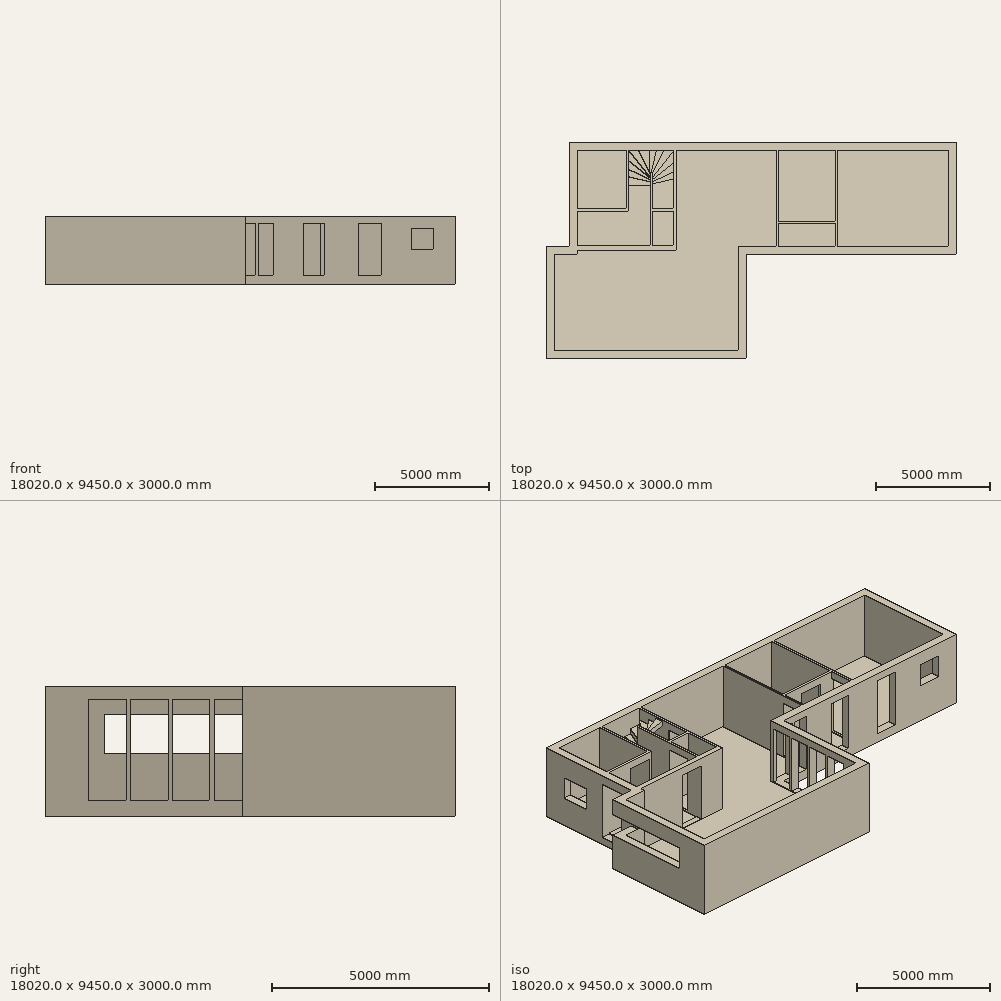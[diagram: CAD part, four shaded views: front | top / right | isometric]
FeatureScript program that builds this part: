
annotation { "Feature Type Name" : "Feature", "Feature Type Description" : "" }
export const myFeature = defineFeature(function(context is Context, id is Id, definition is map)
    precondition{}
    {
        {
            var Q0;
            Q0=qCreatedBy(makeId("Top.planeOp"),FACE);
            var sketch = newSketch(context, id + "F0", { "sketchPlane" : qUnion([Q0])});
            skLineSegment(sketch, "E0", {"start": v(1000, 0) * mm, "end": v(18020, 0) * mm});
            skLineSegment(sketch, "E1", {"start": v(18020, 0) * mm, "end": v(18020, -4900) * mm});
            skLineSegment(sketch, "E2", {"start": v(18020, -4900) * mm, "end": v(8800, -4900) * mm});
            skLineSegment(sketch, "E3", {"start": v(8800, -4900) * mm, "end": v(8800, -9450) * mm});
            skLineSegment(sketch, "E4", {"start": v(8800, -9450) * mm, "end": v(0, -9450) * mm});
            skLineSegment(sketch, "E5", {"start": v(0, -9450) * mm, "end": v(0, -4550) * mm});
            skLineSegment(sketch, "E6", {"start": v(1000, 0) * mm, "end": v(1000, -4550) * mm});
            skLineSegment(sketch, "E7", {"start": v(1000, -4550) * mm, "end": v(0, -4550) * mm});
            skSolve(sketch);
        }
        {
            var Q0;
            Q0 = qSketchRegion(id + "F0", true);
            extrude(context, id + "F1", {"entities" : qUnion([Q0]), "depth" : 3000 * mm, "offsetDistance" : 25 * mm});
        }
        {
            var Q0;
            Q0=makeQuery(id+"F1.opExtrude","CAP_FACE",FACE,{"disambiguationData":[OSD([sQuery(id+"F0.wireOp",EDGE,"E0"),sQuery(id+"F0.wireOp",EDGE,"E1"),sQuery(id+"F0.wireOp",EDGE,"E2"),sQuery(id+"F0.wireOp",EDGE,"E3"),sQuery(id+"F0.wireOp",EDGE,"E4"),sQuery(id+"F0.wireOp",EDGE,"E5")])],"isStart":false});
            shell(context, id + "F2", {"entities" : qUnion([Q0]), "thickness" : 350 * mm});
        }
        {
            var Q0;
            Q0=makeQuery(id+"F2.opShell","OFFSET_FACE",FACE,{"disambiguationData":[OSD([sQuery(id+"F0.wireOp",EDGE,"E0"),sQuery(id+"F0.wireOp",EDGE,"E1"),sQuery(id+"F0.wireOp",EDGE,"E2"),sQuery(id+"F0.wireOp",EDGE,"E3"),sQuery(id+"F0.wireOp",EDGE,"E4"),sQuery(id+"F0.wireOp",EDGE,"E5")])]});
            var sketch = newSketch(context, id + "F3", { "sketchPlane" : qUnion([Q0])});
            skLineSegment(sketch, "E8.bottom", {"start": v(1350, -4500) * mm, "end": v(5700, -4500) * mm});
            skLineSegment(sketch, "E8.top", {"start": v(1350, -4700) * mm, "end": v(5700, -4700) * mm});
            skLineSegment(sketch, "E8.left", {"start": v(1350, -4500) * mm, "end": v(1350, -4700) * mm});
            skLineSegment(sketch, "E8.right", {"start": v(5700, -4500) * mm, "end": v(5700, -4700) * mm});
            skLineSegment(sketch, "E9.bottom", {"start": v(5700, -4500) * mm, "end": v(5600, -4500) * mm});
            skLineSegment(sketch, "E9.top", {"start": v(5700, -350) * mm, "end": v(5600, -350) * mm});
            skLineSegment(sketch, "E9.left", {"start": v(5700, -4500) * mm, "end": v(5700, -350) * mm});
            skLineSegment(sketch, "E9.right", {"start": v(5600, -4500) * mm, "end": v(5600, -350) * mm});
            skLineSegment(sketch, "E10.bottom", {"start": v(1350, -3000) * mm, "end": v(3600, -3000) * mm});
            skLineSegment(sketch, "E10.top", {"start": v(1350, -2900) * mm, "end": v(3600, -2900) * mm});
            skLineSegment(sketch, "E10.left", {"start": v(1350, -3000) * mm, "end": v(1350, -2900) * mm});
            skLineSegment(sketch, "E10.right", {"start": v(3600, -3000) * mm, "end": v(3600, -2900) * mm});
            skLineSegment(sketch, "E11.bottom", {"start": v(3600, -2900) * mm, "end": v(3500, -2900) * mm});
            skLineSegment(sketch, "E11.top", {"start": v(3600, -350) * mm, "end": v(3500, -350) * mm});
            skLineSegment(sketch, "E11.left", {"start": v(3600, -2900) * mm, "end": v(3600, -350) * mm});
            skLineSegment(sketch, "E11.right", {"start": v(3500, -2900) * mm, "end": v(3500, -350) * mm});
            skLineSegment(sketch, "E12.bottom", {"start": v(5600, -3000) * mm, "end": v(4550, -3000) * mm});
            skLineSegment(sketch, "E12.top", {"start": v(5600, -2900) * mm, "end": v(4550, -2900) * mm});
            skLineSegment(sketch, "E12.left", {"start": v(5600, -3000) * mm, "end": v(5600, -2900) * mm});
            skLineSegment(sketch, "E12.right", {"start": v(4550, -3000) * mm, "end": v(4550, -2900) * mm});
            skLineSegment(sketch, "E13.bottom", {"start": v(4550, -3000) * mm, "end": v(4650, -3000) * mm});
            skLineSegment(sketch, "E13.top", {"start": v(4550, -4500) * mm, "end": v(4650, -4500) * mm});
            skLineSegment(sketch, "E13.left", {"start": v(4550, -3000) * mm, "end": v(4550, -4500) * mm});
            skLineSegment(sketch, "E13.right", {"start": v(4650, -3000) * mm, "end": v(4650, -4500) * mm});
            skLineSegment(sketch, "E14.bottom", {"start": v(10200, -4550) * mm, "end": v(10100, -4550) * mm});
            skLineSegment(sketch, "E14.top", {"start": v(10200, -350) * mm, "end": v(10100, -350) * mm});
            skLineSegment(sketch, "E14.left", {"start": v(10200, -4550) * mm, "end": v(10200, -350) * mm});
            skLineSegment(sketch, "E14.right", {"start": v(10100, -4550) * mm, "end": v(10100, -350) * mm});
            skLineSegment(sketch, "E15.bottom", {"start": v(12800, -4550) * mm, "end": v(12700, -4550) * mm});
            skLineSegment(sketch, "E15.top", {"start": v(12800, -350) * mm, "end": v(12700, -350) * mm});
            skLineSegment(sketch, "E15.left", {"start": v(12800, -4550) * mm, "end": v(12800, -350) * mm});
            skLineSegment(sketch, "E15.right", {"start": v(12700, -4550) * mm, "end": v(12700, -350) * mm});
            skLineSegment(sketch, "E16.bottom", {"start": v(10200, -3550) * mm, "end": v(12700, -3550) * mm});
            skLineSegment(sketch, "E16.top", {"start": v(10200, -3450) * mm, "end": v(12700, -3450) * mm});
            skLineSegment(sketch, "E16.left", {"start": v(10200, -3550) * mm, "end": v(10200, -3450) * mm});
            skLineSegment(sketch, "E16.right", {"start": v(12700, -3550) * mm, "end": v(12700, -3450) * mm});
            skLineSegment(sketch, "E17.bottom", {"start": v(4550, -2900) * mm, "end": v(4650, -2900) * mm});
            skLineSegment(sketch, "E17.top", {"start": v(4550, -1300) * mm, "end": v(4650, -1300) * mm});
            skLineSegment(sketch, "E17.left", {"start": v(4550, -2900) * mm, "end": v(4550, -1300) * mm});
            skLineSegment(sketch, "E17.right", {"start": v(4650, -2900) * mm, "end": v(4650, -1300) * mm});
            skSolve(sketch);
        }
        {
            var Q0;
            Q0 = qSketchRegion(id + "F3", true);
            var Q1;
            Q1=makeQuery(id+"F1.opExtrude","CAP_FACE",FACE,{"disambiguationData":[OSD([sQuery(id+"F0.wireOp",EDGE,"E0"),sQuery(id+"F0.wireOp",EDGE,"E1"),sQuery(id+"F0.wireOp",EDGE,"E2"),sQuery(id+"F0.wireOp",EDGE,"E3"),sQuery(id+"F0.wireOp",EDGE,"E4"),sQuery(id+"F0.wireOp",EDGE,"E5")])],"isStart":false});
            extrude(context, id + "F4", {"entities" : qUnion([Q0]), "operationType" : NewBodyOperationType.ADD, "endBound" : BoundingType.UP_TO_SURFACE, "depth" : 25 * mm, "endBoundEntityFace" : qUnion([Q1]), "offsetDistance" : 25 * mm});
        }
        {
            var Q0;
            {var subQ0=sQuery(id+"F0.wireOp",EDGE,"E4");var subQ1=sQuery(id+"F0.wireOp",EDGE,"E5");Q0=makeQuery(id+"F4.boolean.opBoolean","SPLIT",FACE,{"disambiguationData":[TD([makeQuery(id+"F2.opShell","OFFSET_FACE",FACE,{"disambiguationData":[OSD([subQ0])]})])],"derivedFrom":makeQuery(id+"F2.opShell","OFFSET_FACE",FACE,{"disambiguationData":[OSD([subQ1])]})});}
            var sketch = newSketch(context, id + "F5", { "sketchPlane" : qUnion([Q0])});
            skLineSegment(sketch, "E18.bottom", {"start": v(-4550, 1445.43) * mm, "end": v(-8100, 1445.43) * mm});
            skLineSegment(sketch, "E18.top", {"start": v(-4550, 2345.43) * mm, "end": v(-8100, 2345.43) * mm});
            skLineSegment(sketch, "E18.left", {"start": v(-4550, 1445.43) * mm, "end": v(-4550, 2345.43) * mm});
            skLineSegment(sketch, "E18.right", {"start": v(-8100, 1445.43) * mm, "end": v(-8100, 2345.43) * mm});
            skLineSegment(sketch, "E19.bottom", {"start": v(-4000, 380) * mm, "end": v(-3000, 380) * mm});
            skLineSegment(sketch, "E19.top", {"start": v(-4000, 2690) * mm, "end": v(-3000, 2690) * mm});
            skLineSegment(sketch, "E19.left", {"start": v(-4000, 380) * mm, "end": v(-4000, 2690) * mm});
            skLineSegment(sketch, "E19.right", {"start": v(-3000, 380) * mm, "end": v(-3000, 2690) * mm});
            skLineSegment(sketch, "E20.bottom", {"start": v(-2150, 2381.18) * mm, "end": v(-950, 2381.18) * mm});
            skLineSegment(sketch, "E20.top", {"start": v(-2150, 1481.18) * mm, "end": v(-950, 1481.18) * mm});
            skLineSegment(sketch, "E20.left", {"start": v(-2150, 2381.18) * mm, "end": v(-2150, 1481.18) * mm});
            skLineSegment(sketch, "E20.right", {"start": v(-950, 2381.18) * mm, "end": v(-950, 1481.18) * mm});
            skSolve(sketch);
        }
        {
            var Q0;
            Q0 = qSketchRegion(id + "F5", true);
            extrude(context, id + "F6", {"entities" : qUnion([Q0]), "operationType" : NewBodyOperationType.REMOVE, "endBound" : BoundingType.THROUGH_ALL, "oppositeDirection" : true, "depth" : 25 * mm, "offsetDistance" : 25 * mm});
        }
        {
            var Q0;
            Q0=makeQuery(id+"F4.opExtrude","SWEPT_FACE",FACE,{"disambiguationData":[OSD([sQuery(id+"F3.wireOp",EDGE,"E10.bottom")])]});
            var sketch = newSketch(context, id + "F7", { "sketchPlane" : qUnion([Q0])});
            skLineSegment(sketch, "E21.bottom", {"start": v(3500, 380) * mm, "end": v(2500, 380) * mm});
            skLineSegment(sketch, "E21.top", {"start": v(3500, 2690) * mm, "end": v(2500, 2690) * mm});
            skLineSegment(sketch, "E21.left", {"start": v(3500, 380) * mm, "end": v(3500, 2690) * mm});
            skLineSegment(sketch, "E21.right", {"start": v(2500, 380) * mm, "end": v(2500, 2690) * mm});
            skSolve(sketch);
        }
        {
            var Q0;
            Q0 = qSketchRegion(id + "F7", true);
            extrude(context, id + "F8", {"entities" : qUnion([Q0]), "operationType" : NewBodyOperationType.REMOVE, "endBound" : BoundingType.UP_TO_NEXT, "oppositeDirection" : true, "depth" : 25 * mm, "offsetDistance" : 25 * mm});
        }
        {
            var Q0;
            Q0=makeQuery(id+"F4.opExtrude","SWEPT_FACE",FACE,{"disambiguationData":[OSD([sQuery(id+"F3.wireOp",EDGE,"E12.right"),sQuery(id+"F3.wireOp",EDGE,"E13.left")])]});
            var sketch = newSketch(context, id + "F9", { "sketchPlane" : qUnion([Q0])});
            skLineSegment(sketch, "E22.bottom", {"start": v(4000, 380) * mm, "end": v(3000, 380) * mm});
            skLineSegment(sketch, "E22.top", {"start": v(4000, 2690) * mm, "end": v(3000, 2690) * mm});
            skLineSegment(sketch, "E22.left", {"start": v(4000, 380) * mm, "end": v(4000, 2690) * mm});
            skLineSegment(sketch, "E22.right", {"start": v(3000, 380) * mm, "end": v(3000, 2690) * mm});
            skSolve(sketch);
        }
        {
            var Q0;
            Q0 = qSketchRegion(id + "F9", true);
            extrude(context, id + "F10", {"entities" : qUnion([Q0]), "operationType" : NewBodyOperationType.REMOVE, "endBound" : BoundingType.UP_TO_NEXT, "oppositeDirection" : true, "depth" : 25 * mm, "offsetDistance" : 25 * mm});
        }
        {
            var Q0;
            Q0=makeQuery(id+"F4.opExtrude","SWEPT_FACE",FACE,{"disambiguationData":[OSD([sQuery(id+"F3.wireOp",EDGE,"E8.top")])]});
            extrude(context, id + "F11", {"entities" : qUnion([Q0]), "operationType" : NewBodyOperationType.ADD, "depth" : 25 * mm, "offsetDistance" : 25 * mm});
        }
        {
            var Q0;
            Q0=makeQuery(id+"F11.opExtrude","CAP_FACE",FACE,{"disambiguationData":[OSD([sQuery(id+"F3.wireOp",EDGE,"E8.top")])],"isStart":false});
            var sketch = newSketch(context, id + "F12", { "sketchPlane" : qUnion([Q0])});
            skLineSegment(sketch, "E23.bottom", {"start": v(4550, 380) * mm, "end": v(3550, 380) * mm});
            skLineSegment(sketch, "E23.top", {"start": v(4550, 2690) * mm, "end": v(3550, 2690) * mm});
            skLineSegment(sketch, "E23.left", {"start": v(4550, 380) * mm, "end": v(4550, 2690) * mm});
            skLineSegment(sketch, "E23.right", {"start": v(3550, 380) * mm, "end": v(3550, 2690) * mm});
            skSolve(sketch);
        }
        {
            var Q0;
            Q0 = qSketchRegion(id + "F12", true);
            extrude(context, id + "F13", {"entities" : qUnion([Q0]), "operationType" : NewBodyOperationType.REMOVE, "endBound" : BoundingType.UP_TO_NEXT, "oppositeDirection" : true, "depth" : 25 * mm, "offsetDistance" : 25 * mm});
        }
        {
            var Q0;
            Q0=makeQuery(id+"F2.opShell","OFFSET_FACE",FACE,{"disambiguationData":[OSD([sQuery(id+"F0.wireOp",EDGE,"E3")])]});
            var sketch = newSketch(context, id + "F14", { "sketchPlane" : qUnion([Q0])});
            skLineSegment(sketch, "E24.bottom", {"start": v(4700, 380) * mm, "end": v(5562.5, 380) * mm});
            skLineSegment(sketch, "E24.top", {"start": v(4700, 2690) * mm, "end": v(5562.5, 2690) * mm});
            skLineSegment(sketch, "E24.left", {"start": v(4700, 380) * mm, "end": v(4700, 2690) * mm});
            skLineSegment(sketch, "E24.right", {"start": v(5562.5, 380) * mm, "end": v(5562.5, 2690) * mm});
            skLineSegment(sketch, "E25.bottom", {"start": v(5662.5, 380) * mm, "end": v(6525, 380) * mm});
            skLineSegment(sketch, "E25.top", {"start": v(5662.5, 2690) * mm, "end": v(6525, 2690) * mm});
            skLineSegment(sketch, "E25.left", {"start": v(5662.5, 380) * mm, "end": v(5662.5, 2690) * mm});
            skLineSegment(sketch, "E25.right", {"start": v(6525, 380) * mm, "end": v(6525, 2690) * mm});
            skLineSegment(sketch, "E26.bottom", {"start": v(6625, 380) * mm, "end": v(7487.5, 380) * mm});
            skLineSegment(sketch, "E26.top", {"start": v(6625, 2690) * mm, "end": v(7487.5, 2690) * mm});
            skLineSegment(sketch, "E26.left", {"start": v(6625, 380) * mm, "end": v(6625, 2690) * mm});
            skLineSegment(sketch, "E26.right", {"start": v(7487.5, 380) * mm, "end": v(7487.5, 2690) * mm});
            skLineSegment(sketch, "E27.bottom", {"start": v(7587.5, 380) * mm, "end": v(8450, 380) * mm});
            skLineSegment(sketch, "E27.top", {"start": v(7587.5, 2690) * mm, "end": v(8450, 2690) * mm});
            skLineSegment(sketch, "E27.left", {"start": v(7587.5, 380) * mm, "end": v(7587.5, 2690) * mm});
            skLineSegment(sketch, "E27.right", {"start": v(8450, 380) * mm, "end": v(8450, 2690) * mm});
            skSolve(sketch);
        }
        {
            var Q0;
            Q0 = qSketchRegion(id + "F14", true);
            extrude(context, id + "F15", {"entities" : qUnion([Q0]), "operationType" : NewBodyOperationType.REMOVE, "oppositeDirection" : true, "depth" : 350 * mm, "offsetDistance" : 25 * mm});
        }
        {
            var Q0;
            Q0=makeQuery(id+"F1.opExtrude","SWEPT_FACE",FACE,{"disambiguationData":[OSD([sQuery(id+"F0.wireOp",EDGE,"E2")])]});
            var sketch = newSketch(context, id + "F16", { "sketchPlane" : qUnion([Q0])});
            skLineSegment(sketch, "E28.bottom", {"start": v(8600, 2690) * mm, "end": v(9250, 2690) * mm});
            skLineSegment(sketch, "E28.top", {"start": v(8600, 380) * mm, "end": v(9250, 380) * mm});
            skLineSegment(sketch, "E28.left", {"start": v(8600, 2690) * mm, "end": v(8600, 380) * mm});
            skLineSegment(sketch, "E28.right", {"start": v(9250, 2690) * mm, "end": v(9250, 380) * mm});
            skLineSegment(sketch, "E29.bottom", {"start": v(9350, 380) * mm, "end": v(10000, 380) * mm});
            skLineSegment(sketch, "E29.top", {"start": v(9350, 2690) * mm, "end": v(10000, 2690) * mm});
            skLineSegment(sketch, "E29.left", {"start": v(9350, 380) * mm, "end": v(9350, 2690) * mm});
            skLineSegment(sketch, "E29.right", {"start": v(10000, 380) * mm, "end": v(10000, 2690) * mm});
            skSolve(sketch);
        }
        {
            var Q0;
            Q0 = qSketchRegion(id + "F16", true);
            extrude(context, id + "F17", {"entities" : qUnion([Q0]), "operationType" : NewBodyOperationType.REMOVE, "oppositeDirection" : true, "depth" : 350 * mm, "offsetDistance" : 25 * mm});
        }
        {
            var Q0;
            Q0=makeQuery(id+"F4.opExtrude","SWEPT_FACE",FACE,{"disambiguationData":[OSD([sQuery(id+"F3.wireOp",EDGE,"E14.right")])]});
            var sketch = newSketch(context, id + "F18", { "sketchPlane" : qUnion([Q0])});
            skLineSegment(sketch, "E30.bottom", {"start": v(4550, 380) * mm, "end": v(3550, 380) * mm});
            skLineSegment(sketch, "E30.top", {"start": v(4550, 2690) * mm, "end": v(3550, 2690) * mm});
            skLineSegment(sketch, "E30.left", {"start": v(4550, 380) * mm, "end": v(4550, 2690) * mm});
            skLineSegment(sketch, "E30.right", {"start": v(3550, 380) * mm, "end": v(3550, 2690) * mm});
            skSolve(sketch);
        }
        {
            var Q0;
            Q0 = qSketchRegion(id + "F18", true);
            extrude(context, id + "F19", {"entities" : qUnion([Q0]), "operationType" : NewBodyOperationType.REMOVE, "oppositeDirection" : true, "depth" : 100 * mm, "offsetDistance" : 25 * mm});
        }
        {
            var Q0;
            Q0=makeQuery(id+"F4.opExtrude","SWEPT_FACE",FACE,{"disambiguationData":[OSD([sQuery(id+"F3.wireOp",EDGE,"E15.left")])]});
            var sketch = newSketch(context, id + "F20", { "sketchPlane" : qUnion([Q0])});
            skLineSegment(sketch, "E31.bottom", {"start": v(-4550, 380) * mm, "end": v(-3550, 380) * mm});
            skLineSegment(sketch, "E31.top", {"start": v(-4550, 2690) * mm, "end": v(-3550, 2690) * mm});
            skLineSegment(sketch, "E31.left", {"start": v(-4550, 380) * mm, "end": v(-4550, 2690) * mm});
            skLineSegment(sketch, "E31.right", {"start": v(-3550, 380) * mm, "end": v(-3550, 2690) * mm});
            skSolve(sketch);
        }
        {
            var Q0;
            Q0 = qSketchRegion(id + "F20", true);
            extrude(context, id + "F21", {"entities" : qUnion([Q0]), "operationType" : NewBodyOperationType.REMOVE, "endBound" : BoundingType.UP_TO_NEXT, "oppositeDirection" : true, "depth" : 25 * mm, "offsetDistance" : 25 * mm});
        }
        {
            var Q0;
            Q0=makeQuery(id+"F1.opExtrude","SWEPT_FACE",FACE,{"disambiguationData":[OSD([sQuery(id+"F0.wireOp",EDGE,"E2")])]});
            var sketch = newSketch(context, id + "F22", { "sketchPlane" : qUnion([Q0])});
            skLineSegment(sketch, "E32.bottom", {"start": v(11350, 380) * mm, "end": v(12250, 380) * mm});
            skLineSegment(sketch, "E32.top", {"start": v(11350, 2690) * mm, "end": v(12250, 2690) * mm});
            skLineSegment(sketch, "E32.left", {"start": v(11350, 380) * mm, "end": v(11350, 2690) * mm});
            skLineSegment(sketch, "E32.right", {"start": v(12250, 380) * mm, "end": v(12250, 2690) * mm});
            skLineSegment(sketch, "E33.bottom", {"start": v(16070, 2448.05) * mm, "end": v(17070, 2448.05) * mm});
            skLineSegment(sketch, "E33.top", {"start": v(16070, 1548.05) * mm, "end": v(17070, 1548.05) * mm});
            skLineSegment(sketch, "E33.left", {"start": v(16070, 2448.05) * mm, "end": v(16070, 1548.05) * mm});
            skLineSegment(sketch, "E33.right", {"start": v(17070, 2448.05) * mm, "end": v(17070, 1548.05) * mm});
            skLineSegment(sketch, "E34.bottom", {"start": v(13770, 2690) * mm, "end": v(14770, 2690) * mm});
            skLineSegment(sketch, "E34.top", {"start": v(13770, 380) * mm, "end": v(14770, 380) * mm});
            skLineSegment(sketch, "E34.left", {"start": v(13770, 2690) * mm, "end": v(13770, 380) * mm});
            skLineSegment(sketch, "E34.right", {"start": v(14770, 2690) * mm, "end": v(14770, 380) * mm});
            skSolve(sketch);
        }
        {
            var Q0;
            Q0 = qSketchRegion(id + "F22", true);
            extrude(context, id + "F23", {"entities" : qUnion([Q0]), "operationType" : NewBodyOperationType.REMOVE, "endBound" : BoundingType.UP_TO_NEXT, "oppositeDirection" : true, "depth" : 25 * mm, "offsetDistance" : 25 * mm});
        }
        {
            var Q0;
            Q0=makeQuery(id+"F4.opExtrude","SWEPT_FACE",FACE,{"disambiguationData":[OSD([sQuery(id+"F3.wireOp",EDGE,"E16.bottom")])]});
            var sketch = newSketch(context, id + "F24", { "sketchPlane" : qUnion([Q0])});
            skLineSegment(sketch, "E35.bottom", {"start": v(11100, 380) * mm, "end": v(12100, 380) * mm});
            skLineSegment(sketch, "E35.top", {"start": v(11100, 2690) * mm, "end": v(12100, 2690) * mm});
            skLineSegment(sketch, "E35.left", {"start": v(11100, 380) * mm, "end": v(11100, 2690) * mm});
            skLineSegment(sketch, "E35.right", {"start": v(12100, 380) * mm, "end": v(12100, 2690) * mm});
            skSolve(sketch);
        }
        {
            var Q0;
            Q0 = qSketchRegion(id + "F24", true);
            extrude(context, id + "F25", {"entities" : qUnion([Q0]), "operationType" : NewBodyOperationType.REMOVE, "endBound" : BoundingType.UP_TO_NEXT, "oppositeDirection" : true, "depth" : 25 * mm, "offsetDistance" : 25 * mm});
        }
        {
            var Q0;
            {var subQ0=sQuery(id+"F3.wireOp",EDGE,"E8.right");Q0=makeQuery(id+"F11.boolean.opBoolean","MERGE",FACE,{"derivedFrom":[makeQuery(id+"F4.opExtrude","SWEPT_FACE",FACE,{"disambiguationData":[OSD([subQ0,sQuery(id+"F3.wireOp",EDGE,"E9.left")])]}),makeQuery(id+"F11.opExtrude","SWEPT_FACE",FACE,{"disambiguationData":[OSD([sQuery(id+"F3.wireOp",EDGE,"E8.top"),subQ0])]})]});}
            var sketch = newSketch(context, id + "F26", { "sketchPlane" : qUnion([Q0])});
            skLineSegment(sketch, "E36.bottom", {"start": v(-1900, 380) * mm, "end": v(-2900, 380) * mm});
            skLineSegment(sketch, "E36.top", {"start": v(-1900, 2690) * mm, "end": v(-2900, 2690) * mm});
            skLineSegment(sketch, "E36.left", {"start": v(-1900, 380) * mm, "end": v(-1900, 2690) * mm});
            skLineSegment(sketch, "E36.right", {"start": v(-2900, 380) * mm, "end": v(-2900, 2690) * mm});
            skSolve(sketch);
        }
        {
            var Q0;
            Q0 = qSketchRegion(id + "F26", true);
            extrude(context, id + "F27", {"entities" : qUnion([Q0]), "operationType" : NewBodyOperationType.REMOVE, "endBound" : BoundingType.UP_TO_NEXT, "oppositeDirection" : true, "depth" : 25 * mm, "offsetDistance" : 25 * mm});
        }
        {
            var Q0;
            {var subQ1=sQuery(id+"F0.wireOp",EDGE,"E5");var subQ4=sQuery(id+"F0.wireOp",EDGE,"E0");Q0=makeQuery(id+"F4.boolean.opBoolean","SPLIT",FACE,{"disambiguationData":[TD([makeQuery(id+"F4.opExtrude","SWEPT_FACE",FACE,{"disambiguationData":[OSD([sQuery(id+"F3.wireOp",EDGE,"E10.bottom")])]})])],"derivedFrom":makeQuery(id+"F2.opShell","OFFSET_FACE",FACE,{"disambiguationData":[OSD([subQ4,sQuery(id+"F0.wireOp",EDGE,"E1"),sQuery(id+"F0.wireOp",EDGE,"E2"),sQuery(id+"F0.wireOp",EDGE,"E3"),sQuery(id+"F0.wireOp",EDGE,"E4"),subQ1])]})});}
            var sketch = newSketch(context, id + "F28", { "sketchPlane" : qUnion([Q0])});
            skLineSegment(sketch, "E37", {"start": v(4550, -1850) * mm, "end": v(3600, -1850) * mm});
            skLineSegment(sketch, "E38", {"start": v(3600, -1850) * mm, "end": v(3600, -1477.18) * mm});
            skLineSegment(sketch, "E39", {"start": v(3600, -1477.18) * mm, "end": v(4550, -1694) * mm});
            skLineSegment(sketch, "E40", {"start": v(4550, -1694) * mm, "end": v(4550, -1850) * mm});
            skSolve(sketch);
        }
        {
            var Q0;
            Q0 = qSketchRegion(id + "F28", true);
            extrude(context, id + "F29", {"entities" : qUnion([Q0]), "operationType" : NewBodyOperationType.ADD, "depth" : (3000 / 14) * mm, "offsetDistance" : 25 * mm});
        }
        {
            var Q0;
            Q0=makeQuery(id+"F29.opExtrude","CAP_FACE",FACE,{"disambiguationData":[OSD([sQuery(id+"F28.wireOp",EDGE,"E37"),sQuery(id+"F28.wireOp",EDGE,"E38"),sQuery(id+"F28.wireOp",EDGE,"E39"),sQuery(id+"F28.wireOp",EDGE,"E40")])],"isStart":false});
            var sketch = newSketch(context, id + "F30", { "sketchPlane" : qUnion([Q0])});
            skLineSegment(sketch, "E41", {"start": v(3600, -1487.43) * mm, "end": v(4550, -1704.26) * mm});
            skLineSegment(sketch, "E42", {"start": v(4550, -1704.26) * mm, "end": v(4550, -1601.6) * mm});
            skLineSegment(sketch, "E43", {"start": v(4550, -1601.6) * mm, "end": v(3600, -1144.1) * mm});
            skLineSegment(sketch, "E44", {"start": v(3600, -1144.1) * mm, "end": v(3600, -1487.43) * mm});
            skSolve(sketch);
        }
        {
            var Q0;
            Q0 = qSketchRegion(id + "F30", true);
            extrude(context, id + "F31", {"entities" : qUnion([Q0]), "operationType" : NewBodyOperationType.ADD, "depth" : (3000 / 14) * mm, "offsetDistance" : 25 * mm});
        }
        {
            var Q0;
            Q0=makeQuery(id+"F31.opExtrude","CAP_FACE",FACE,{"disambiguationData":[OSD([sQuery(id+"F30.wireOp",EDGE,"E41"),sQuery(id+"F30.wireOp",EDGE,"E42"),sQuery(id+"F30.wireOp",EDGE,"E43"),sQuery(id+"F30.wireOp",EDGE,"E44")])],"isStart":false});
            var sketch = newSketch(context, id + "F32", { "sketchPlane" : qUnion([Q0])});
            skLineSegment(sketch, "E45", {"start": v(3600, -1155.2) * mm, "end": v(4550, -1612.7) * mm});
            skLineSegment(sketch, "E46", {"start": v(4550, -1612.7) * mm, "end": v(4550, -1519.02) * mm});
            skLineSegment(sketch, "E47", {"start": v(4550, -1519.02) * mm, "end": v(3600, -761.42) * mm});
            skLineSegment(sketch, "E48", {"start": v(3600, -761.42) * mm, "end": v(3600, -1155.2) * mm});
            skSolve(sketch);
        }
        {
            var Q0;
            Q0 = qSketchRegion(id + "F32", true);
            extrude(context, id + "F33", {"entities" : qUnion([Q0]), "operationType" : NewBodyOperationType.ADD, "depth" : (3000 / 14) * mm, "offsetDistance" : 25 * mm});
        }
        {
            var Q0;
            Q0=makeQuery(id+"F33.opExtrude","CAP_FACE",FACE,{"disambiguationData":[OSD([sQuery(id+"F32.wireOp",EDGE,"E45"),sQuery(id+"F32.wireOp",EDGE,"E46"),sQuery(id+"F32.wireOp",EDGE,"E47"),sQuery(id+"F32.wireOp",EDGE,"E48")])],"isStart":false});
            var sketch = newSketch(context, id + "F34", { "sketchPlane" : qUnion([Q0])});
            skLineSegment(sketch, "E49", {"start": v(4550, -1531.81) * mm, "end": v(3600, -774.21) * mm});
            skLineSegment(sketch, "E50", {"start": v(3600, -774.21) * mm, "end": v(3600, -350) * mm});
            skLineSegment(sketch, "E51", {"start": v(3643.89, -350) * mm, "end": v(4550, -1486.23) * mm});
            skLineSegment(sketch, "E52", {"start": v(4550, -1486.23) * mm, "end": v(4550, -1531.81) * mm});
            skLineSegment(sketch, "E53", {"start": v(3600, -350) * mm, "end": v(3643.89, -350) * mm});
            skSolve(sketch);
        }
        {
            var Q0;
            Q0 = qSketchRegion(id + "F34", true);
            extrude(context, id + "F35", {"entities" : qUnion([Q0]), "operationType" : NewBodyOperationType.ADD, "depth" : (3000 / 14) * mm, "offsetDistance" : 25 * mm});
        }
        {
            var Q0;
            Q0=makeQuery(id+"F35.opExtrude","CAP_FACE",FACE,{"disambiguationData":[OSD([sQuery(id+"F34.wireOp",EDGE,"E49"),sQuery(id+"F34.wireOp",EDGE,"E50"),sQuery(id+"F34.wireOp",EDGE,"E51"),sQuery(id+"F34.wireOp",EDGE,"E52")])],"isStart":false});
            var sketch = newSketch(context, id + "F36", { "sketchPlane" : qUnion([Q0])});
            skLineSegment(sketch, "E54", {"start": v(3631.1, -350) * mm, "end": v(4550, -1502.26) * mm});
            skLineSegment(sketch, "E55", {"start": v(4550, -1502.26) * mm, "end": v(4550, -1337.24) * mm});
            skLineSegment(sketch, "E56", {"start": v(3643.89, -350) * mm, "end": v(4074.57, -350) * mm});
            skLineSegment(sketch, "E57", {"start": v(4074.57, -350) * mm, "end": v(4550, -1337.24) * mm});
            skLineSegment(sketch, "E58", {"start": v(4074.57, -350) * mm, "end": v(3631.1, -350) * mm});
            skSolve(sketch);
        }
        {
            var Q0;
            Q0 = qSketchRegion(id + "F36", true);
            extrude(context, id + "F37", {"entities" : qUnion([Q0]), "operationType" : NewBodyOperationType.ADD, "depth" : (3000 / 14) * mm, "offsetDistance" : 25 * mm});
        }
        {
            var Q0;
            Q0=makeQuery(id+"F37.opExtrude","CAP_FACE",FACE,{"disambiguationData":[OSD([sQuery(id+"F36.wireOp",EDGE,"E54"),sQuery(id+"F36.wireOp",EDGE,"E55"),sQuery(id+"F36.wireOp",EDGE,"NWCFt3wr-qczF-JT4h-rdwd-O4vbqxLeZZzJ"),sQuery(id+"F36.wireOp",EDGE,"E56"),sQuery(id+"F36.wireOp",EDGE,"E57")])],"isStart":false});
            var sketch = newSketch(context, id + "F38", { "sketchPlane" : qUnion([Q0])});
            skLineSegment(sketch, "E59", {"start": v(4063.47, -350) * mm, "end": v(4550, -1360.28) * mm});
            skLineSegment(sketch, "E60", {"start": v(4550, -1360.28) * mm, "end": v(4557.4, -1297.11) * mm});
            skLineSegment(sketch, "E61", {"start": v(4557.4, -1297.11) * mm, "end": v(4557.4, -350) * mm});
            skLineSegment(sketch, "E62", {"start": v(4557.4, -350) * mm, "end": v(4063.47, -350) * mm});
            skSolve(sketch);
        }
        {
            var Q0;
            Q0 = qSketchRegion(id + "F38", true);
            extrude(context, id + "F39", {"entities" : qUnion([Q0]), "operationType" : NewBodyOperationType.ADD, "depth" : (3000 / 14) * mm, "offsetDistance" : 25 * mm});
        }
        {
            var Q0;
            Q0=makeQuery(id+"F39.opExtrude","CAP_FACE",FACE,{"disambiguationData":[OSD([sQuery(id+"F38.wireOp",EDGE,"E59"),sQuery(id+"F38.wireOp",EDGE,"E60"),sQuery(id+"F38.wireOp",EDGE,"E61"),sQuery(id+"F38.wireOp",EDGE,"E62")])],"isStart":false});
            var sketch = newSketch(context, id + "F40", { "sketchPlane" : qUnion([Q0])});
            skLineSegment(sketch, "E63", {"start": v(4620.44, -1302.15) * mm, "end": v(4837.76, -350) * mm});
            skLineSegment(sketch, "E64", {"start": v(4837.76, -350) * mm, "end": v(4547.4, -350) * mm});
            skLineSegment(sketch, "E65", {"start": v(4547.4, -350) * mm, "end": v(4547.4, -1300) * mm});
            skLineSegment(sketch, "E66", {"start": v(4550, -1302.15) * mm, "end": v(4547.4, -1300) * mm});
            skLineSegment(sketch, "E67", {"start": v(4550, -1302.15) * mm, "end": v(4620.44, -1302.15) * mm});
            skSolve(sketch);
        }
        {
            var Q0;
            Q0 = qSketchRegion(id + "F40", true);
            extrude(context, id + "F41", {"entities" : qUnion([Q0]), "operationType" : NewBodyOperationType.ADD, "depth" : (3000 / 14) * mm, "offsetDistance" : 25 * mm});
        }
        {
            var Q0;
            Q0=makeQuery(id+"F41.opExtrude","CAP_FACE",FACE,{"disambiguationData":[OSD([sQuery(id+"F40.wireOp",EDGE,"E63"),sQuery(id+"F40.wireOp",EDGE,"E64"),sQuery(id+"F40.wireOp",EDGE,"E65"),sQuery(id+"F40.wireOp",EDGE,"E66"),sQuery(id+"F40.wireOp",EDGE,"E67")])],"isStart":false});
            var sketch = newSketch(context, id + "F42", { "sketchPlane" : qUnion([Q0])});
            skLineSegment(sketch, "E68", {"start": v(4827.5, -350) * mm, "end": v(5153.82, -350) * mm});
            skLineSegment(sketch, "E69", {"start": v(5153.82, -350) * mm, "end": v(4649.62, -1396.98) * mm});
            skLineSegment(sketch, "E70", {"start": v(4649.62, -1396.98) * mm, "end": v(4588.54, -1396.98) * mm});
            skLineSegment(sketch, "E71", {"start": v(4588.54, -1396.98) * mm, "end": v(4827.5, -350) * mm});
            skSolve(sketch);
        }
        {
            var Q0;
            Q0 = qSketchRegion(id + "F42", true);
            extrude(context, id + "F43", {"entities" : qUnion([Q0]), "operationType" : NewBodyOperationType.ADD, "depth" : (3000 / 14) * mm, "offsetDistance" : 25 * mm});
        }
        {
            var Q0;
            Q0=makeQuery(id+"F43.opExtrude","CAP_FACE",FACE,{"disambiguationData":[OSD([sQuery(id+"F42.wireOp",EDGE,"E68"),sQuery(id+"F42.wireOp",EDGE,"E69"),sQuery(id+"F42.wireOp",EDGE,"E70"),sQuery(id+"F42.wireOp",EDGE,"E71")])],"isStart":false});
            var sketch = newSketch(context, id + "F44", { "sketchPlane" : qUnion([Q0])});
            skLineSegment(sketch, "E72", {"start": v(5142.72, -350) * mm, "end": v(5600, -350) * mm});
            skLineSegment(sketch, "E73", {"start": v(5600, -350) * mm, "end": v(5600, -371.68) * mm});
            skLineSegment(sketch, "E74", {"start": v(5600, -371.68) * mm, "end": v(4648.21, -1565.18) * mm});
            skLineSegment(sketch, "E75", {"start": v(4648.21, -1565.18) * mm, "end": v(4594.6, -1488.16) * mm});
            skLineSegment(sketch, "E76", {"start": v(4594.6, -1488.16) * mm, "end": v(5142.72, -350) * mm});
            skSolve(sketch);
        }
        {
            var Q0;
            Q0 = qSketchRegion(id + "F44", true);
            extrude(context, id + "F45", {"entities" : qUnion([Q0]), "operationType" : NewBodyOperationType.ADD, "depth" : (3000 / 14) * mm, "offsetDistance" : 25 * mm});
        }
        {
            var Q0;
            Q0=makeQuery(id+"F45.opExtrude","CAP_FACE",FACE,{"disambiguationData":[OSD([sQuery(id+"F44.wireOp",EDGE,"E72"),sQuery(id+"F44.wireOp",EDGE,"E73"),sQuery(id+"F44.wireOp",EDGE,"E74"),sQuery(id+"F44.wireOp",EDGE,"E75"),sQuery(id+"F44.wireOp",EDGE,"E76")])],"isStart":false});
            var sketch = newSketch(context, id + "F46", { "sketchPlane" : qUnion([Q0])});
            skLineSegment(sketch, "E77", {"start": v(5600, -355.64) * mm, "end": v(4650, -1546.9) * mm});
            skLineSegment(sketch, "E78", {"start": v(4650, -1546.9) * mm, "end": v(4650, -1651.67) * mm});
            skLineSegment(sketch, "E79", {"start": v(4650, -1651.67) * mm, "end": v(5600, -894.07) * mm});
            skLineSegment(sketch, "E80", {"start": v(5600, -894.07) * mm, "end": v(5600, -355.64) * mm});
            skSolve(sketch);
        }
        {
            var Q0;
            Q0 = qSketchRegion(id + "F46", true);
            extrude(context, id + "F47", {"entities" : qUnion([Q0]), "operationType" : NewBodyOperationType.ADD, "depth" : (3000 / 14) * mm, "offsetDistance" : 25 * mm});
        }
        {
            var Q0;
            Q0=makeQuery(id+"F47.opExtrude","CAP_FACE",FACE,{"disambiguationData":[OSD([sQuery(id+"F46.wireOp",EDGE,"E77"),sQuery(id+"F46.wireOp",EDGE,"E78"),sQuery(id+"F46.wireOp",EDGE,"E79"),sQuery(id+"F46.wireOp",EDGE,"E80")])],"isStart":false});
            var sketch = newSketch(context, id + "F48", { "sketchPlane" : qUnion([Q0])});
            skLineSegment(sketch, "E81", {"start": v(4650, -1638.88) * mm, "end": v(5600, -881.28) * mm});
            skLineSegment(sketch, "E82", {"start": v(5600, -881.28) * mm, "end": v(5600, -1277.43) * mm});
            skLineSegment(sketch, "E83", {"start": v(5600, -1277.43) * mm, "end": v(4650, -1734.92) * mm});
            skLineSegment(sketch, "E84", {"start": v(4650, -1734.92) * mm, "end": v(4650, -1638.88) * mm});
            skSolve(sketch);
        }
        {
            var Q0;
            Q0 = qSketchRegion(id + "F48", true);
            extrude(context, id + "F49", {"entities" : qUnion([Q0]), "operationType" : NewBodyOperationType.ADD, "depth" : (3000 / 14) * mm, "offsetDistance" : 25 * mm});
        }
        {
            var Q0;
            Q0=makeQuery(id+"F49.opExtrude","CAP_FACE",FACE,{"disambiguationData":[OSD([sQuery(id+"F48.wireOp",EDGE,"E81"),sQuery(id+"F48.wireOp",EDGE,"E82"),sQuery(id+"F48.wireOp",EDGE,"E83"),sQuery(id+"F48.wireOp",EDGE,"E84")])],"isStart":false});
            var sketch = newSketch(context, id + "F50", { "sketchPlane" : qUnion([Q0])});
            skLineSegment(sketch, "E85", {"start": v(4650, -1723.83) * mm, "end": v(5600, -1266.33) * mm});
            skLineSegment(sketch, "E86", {"start": v(5600, -1266.33) * mm, "end": v(5600, -1585.5) * mm});
            skLineSegment(sketch, "E87", {"start": v(5600, -1585.5) * mm, "end": v(4650, -1802.32) * mm});
            skLineSegment(sketch, "E88", {"start": v(4650, -1802.32) * mm, "end": v(4650, -1723.83) * mm});
            skSolve(sketch);
        }
        {
            var Q0;
            Q0 = qSketchRegion(id + "F50", true);
            extrude(context, id + "F51", {"entities" : qUnion([Q0]), "operationType" : NewBodyOperationType.ADD, "depth" : (3000 / 14) * mm, "offsetDistance" : 25 * mm});
        }
        {
            var Q0;
            Q0=makeQuery(id+"F1.opExtrude","SWEPT_FACE",FACE,{"disambiguationData":[OSD([sQuery(id+"F0.wireOp",EDGE,"E6")])]});
            var sketch = newSketch(context, id + "F52", { "sketchPlane" : qUnion([Q0])});
            skLineSegment(sketch, "E89.bottom", {"start": v(950, 1183.67) * mm, "end": v(2150, 1183.67) * mm});
            skLineSegment(sketch, "E89.top", {"start": v(950, 2083.67) * mm, "end": v(2150, 2083.67) * mm});
            skLineSegment(sketch, "E89.left", {"start": v(950, 1183.67) * mm, "end": v(950, 2083.67) * mm});
            skLineSegment(sketch, "E89.right", {"start": v(2150, 1183.67) * mm, "end": v(2150, 2083.67) * mm});
            skLineSegment(sketch, "E90.bottom", {"start": v(3000, 320) * mm, "end": v(4000, 320) * mm});
            skLineSegment(sketch, "E90.top", {"start": v(3000, 2630) * mm, "end": v(4000, 2630) * mm});
            skLineSegment(sketch, "E90.left", {"start": v(3000, 320) * mm, "end": v(3000, 2630) * mm});
            skLineSegment(sketch, "E90.right", {"start": v(4000, 320) * mm, "end": v(4000, 2630) * mm});
            skSolve(sketch);
        }
        {
            var Q0;
            Q0 = qSketchRegion(id + "F52", true);
            extrude(context, id + "F53", {"entities" : qUnion([Q0]), "operationType" : NewBodyOperationType.REMOVE, "oppositeDirection" : true, "depth" : 350 * mm, "offsetDistance" : 25 * mm});
        }
        {
            var Q0;
            Q0=makeQuery(id+"F1.opExtrude","SWEPT_FACE",FACE,{"disambiguationData":[OSD([sQuery(id+"F0.wireOp",EDGE,"E7")])]});
            var sketch = newSketch(context, id + "F54", { "sketchPlane" : qUnion([Q0])});
            skLineSegment(sketch, "E91.bottom", {"start": v(-1000, 1445.43) * mm, "end": v(-350, 1445.43) * mm});
            skLineSegment(sketch, "E91.top", {"start": v(-1000, 2345.43) * mm, "end": v(-350, 2345.43) * mm});
            skLineSegment(sketch, "E91.left", {"start": v(-1000, 1445.43) * mm, "end": v(-1000, 2345.43) * mm});
            skLineSegment(sketch, "E91.right", {"start": v(-350, 1445.43) * mm, "end": v(-350, 2345.43) * mm});
            skSolve(sketch);
        }
        {
            var Q0;
            Q0 = qSketchRegion(id + "F54", true);
            extrude(context, id + "F55", {"entities" : qUnion([Q0]), "operationType" : NewBodyOperationType.REMOVE, "endBound" : BoundingType.UP_TO_NEXT, "oppositeDirection" : true, "depth" : 25 * mm, "offsetDistance" : 25 * mm});
        }
    });
